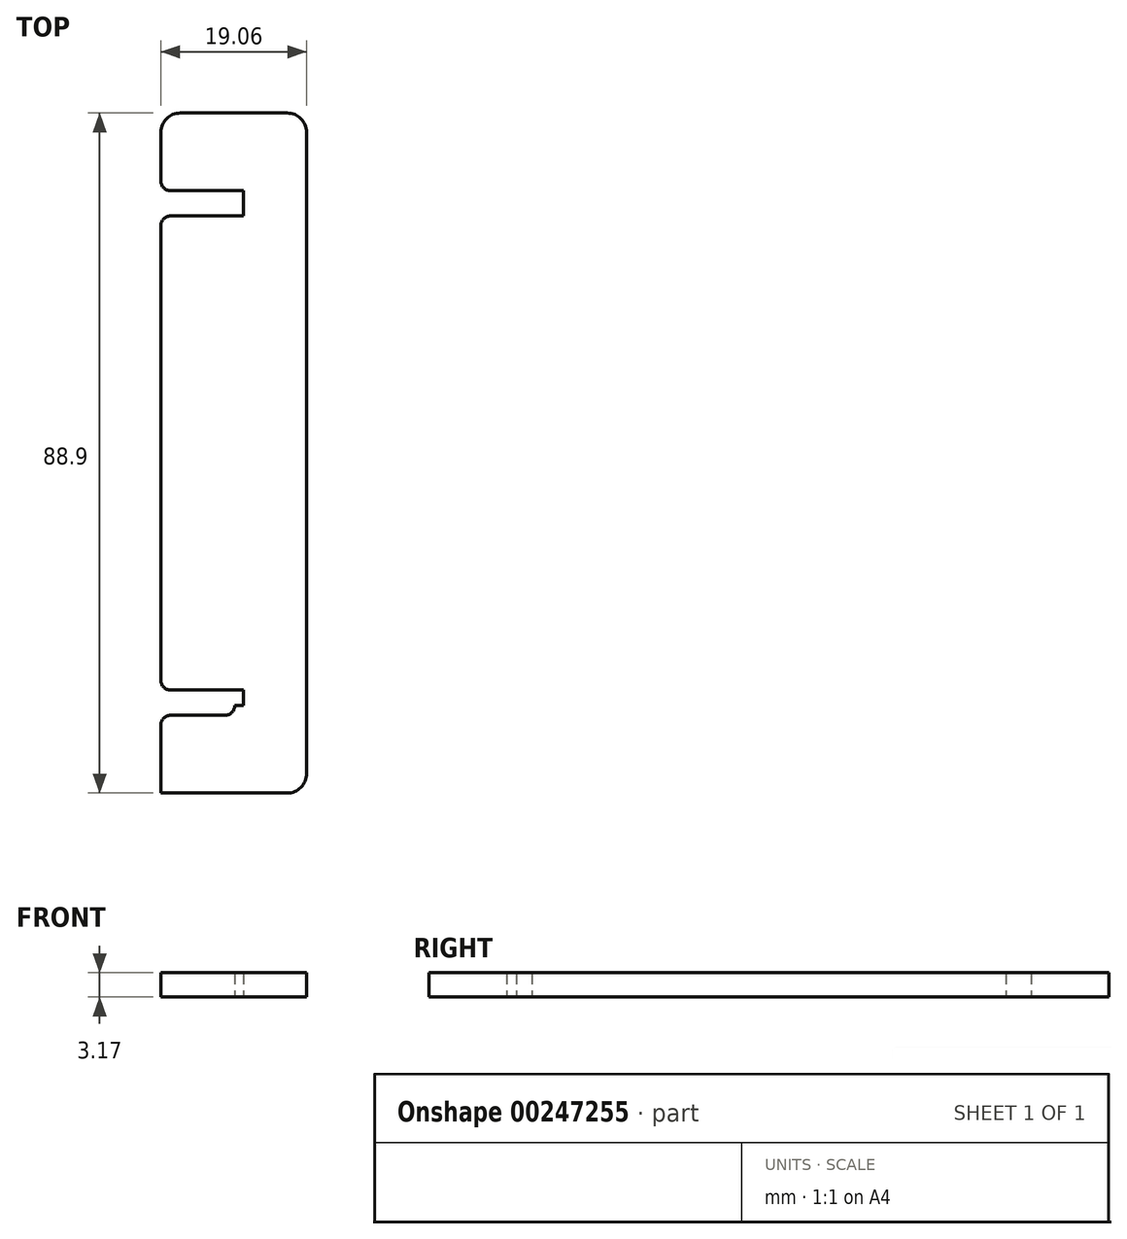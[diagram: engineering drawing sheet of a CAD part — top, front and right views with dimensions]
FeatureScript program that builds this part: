
annotation { "Feature Type Name" : "Feature", "Feature Type Description" : "" }
export const myFeature = defineFeature(function(context is Context, id is Id, definition is map)
    precondition{}
    {
        {
            var Q0;
            Q0=qCreatedBy(makeId("Top.planeOp"),FACE);
            var sketch = newSketch(context, id + "F0", { "sketchPlane" : qUnion([Q0])});
            skLineSegment(sketch, "E0.bottom", {"start": v(-9.52, 44.45) * mm, "end": v(9.53, 44.45) * mm});
            skLineSegment(sketch, "E0.top", {"start": v(-9.53, -44.45) * mm, "end": v(9.52, -44.45) * mm});
            skLineSegment(sketch, "E0.left", {"start": v(-9.52, 44.45) * mm, "end": v(-9.52, 34.3) * mm});
            skLineSegment(sketch, "E0.right", {"start": v(9.53, 44.45) * mm, "end": v(9.52, -44.45) * mm});
            skPoint(sketch, "E0.middle", {"position": v(0, 0) * mm});
            skLineSegment(sketch, "E1", {"start": v(9.52, -44.45) * mm, "end": v(-9.53, -44.45) * mm});
            skLineSegment(sketch, "E2", {"start": v(-9.53, -44.45) * mm, "end": v(-9.53, -34.3) * mm});
            skLineSegment(sketch, "E3.bottom", {"start": v(-9.53, -34.3) * mm, "end": v(0.13, -34.3) * mm});
            skLineSegment(sketch, "E3.top", {"start": v(-9.53, -30.99) * mm, "end": v(0.13, -30.99) * mm});
            skLineSegment(sketch, "E3.right", {"start": v(0.13, -34.3) * mm, "end": v(0.13, -30.99) * mm});
            skLineSegment(sketch, "E4.trimOffspring", {"start": v(-9.53, -34.3) * mm, "end": v(-9.53, -44.45) * mm});
            skLineSegment(sketch, "E5.MirrorCS", {"start": v(-9.53, 30.99) * mm, "end": v(0.13, 30.99) * mm});
            skLineSegment(sketch, "E6.MirrorCS", {"start": v(0.13, 34.3) * mm, "end": v(0.13, 30.99) * mm});
            skLineSegment(sketch, "E7.MirrorCS", {"start": v(-9.52, 34.3) * mm, "end": v(0.13, 34.3) * mm});
            skLineSegment(sketch, "E8.trimOffspring", {"start": v(-9.52, 30.99) * mm, "end": v(-9.53, -30.99) * mm});
            skPoint(sketch, "E9.orphan", {"position": v(-9.53, 0) * mm});
            skPoint(sketch, "E10.end.orphan", {"position": v(9.53, 0) * mm});
            skSolve(sketch);
        }
        {
            var Q0;
            Q0 = qSketchRegion(id + "F0", true);
            extrude(context, id + "F1", {"entities" : qUnion([Q0]), "depth" : 3.17 * mm});
        }
        {
            var Q0;
            Q0=makeQuery(id+"F1.opExtrude","SWEPT_EDGE",EDGE,{"disambiguationData":[OSD([sQuery(id+"F0.wireOp",EDGE,"E0.bottom"),sQuery(id+"F0.wireOp",EDGE,"E0.left")])]});
            var Q1;
            Q1=makeQuery(id+"F1.opExtrude","SWEPT_EDGE",EDGE,{"disambiguationData":[OSD([sQuery(id+"F0.wireOp",EDGE,"E0.bottom"),sQuery(id+"F0.wireOp",EDGE,"E0.right")])]});
            var Q2;
            Q2=makeQuery(id+"F1.opExtrude","SWEPT_EDGE",EDGE,{"disambiguationData":[OSD([sQuery(id+"F0.wireOp",EDGE,"E0.right"),sQuery(id+"F0.wireOp",EDGE,"E1")])]});
            var Q3;
            Q3=makeQuery(id+"F1.opExtrude","SWEPT_EDGE",EDGE,{"disambiguationData":[OSD([sQuery(id+"F0.wireOp",EDGE,"E1"),sQuery(id+"F0.wireOp",EDGE,"E4.trimOffspring")])]});
            fillet(context, id + "F2", {"entities" : qUnion([Q0, Q1, Q2, Q3]), "radius" : 2.54 * mm, "tangentPropagation" : true, "allowEdgeOverflow" : false});
        }
        {
            var Q0;
            Q0=makeQuery(id+"F1.opExtrude","SWEPT_EDGE",EDGE,{"disambiguationData":[OSD([sQuery(id+"F0.wireOp",EDGE,"E0.left"),sQuery(id+"F0.wireOp",EDGE,"E7.MirrorCS")])]});
            var Q1;
            Q1=makeQuery(id+"F1.opExtrude","SWEPT_EDGE",EDGE,{"disambiguationData":[OSD([sQuery(id+"F0.wireOp",EDGE,"E3.top"),sQuery(id+"F0.wireOp",EDGE,"E8.trimOffspring")])]});
            var Q2;
            Q2=makeQuery(id+"F1.opExtrude","SWEPT_EDGE",EDGE,{"disambiguationData":[OSD([sQuery(id+"F0.wireOp",EDGE,"E5.MirrorCS"),sQuery(id+"F0.wireOp",EDGE,"E8.trimOffspring")])]});
            var Q3;
            Q3=makeQuery(id+"F1.opExtrude","SWEPT_EDGE",EDGE,{"disambiguationData":[OSD([sQuery(id+"F0.wireOp",EDGE,"E3.bottom"),sQuery(id+"F0.wireOp",EDGE,"E4.trimOffspring")])]});
            fillet(context, id + "F3", {"entities" : qUnion([Q0, Q1, Q2, Q3]), "radius" : 1.27 * mm, "tangentPropagation" : true, "allowEdgeOverflow" : false});
        }
        {
            var Q0;
            Q0=makeQuery(id+"F1.opExtrude","SWEPT_FACE",FACE,{"disambiguationData":[OSD([sQuery(id+"F0.wireOp",EDGE,"E6.MirrorCS")])]});
            var Q1;
            Q1=makeQuery(id+"F1.opExtrude","SWEPT_FACE",FACE,{"disambiguationData":[OSD([sQuery(id+"F0.wireOp",EDGE,"E3.right")])]});
            extrude(context, id + "F4", {"entities" : qUnion([Q0, Q1]), "operationType" : NewBodyOperationType.REMOVE, "oppositeDirection" : true, "depth" : 1.14 * mm});
        }
    });
